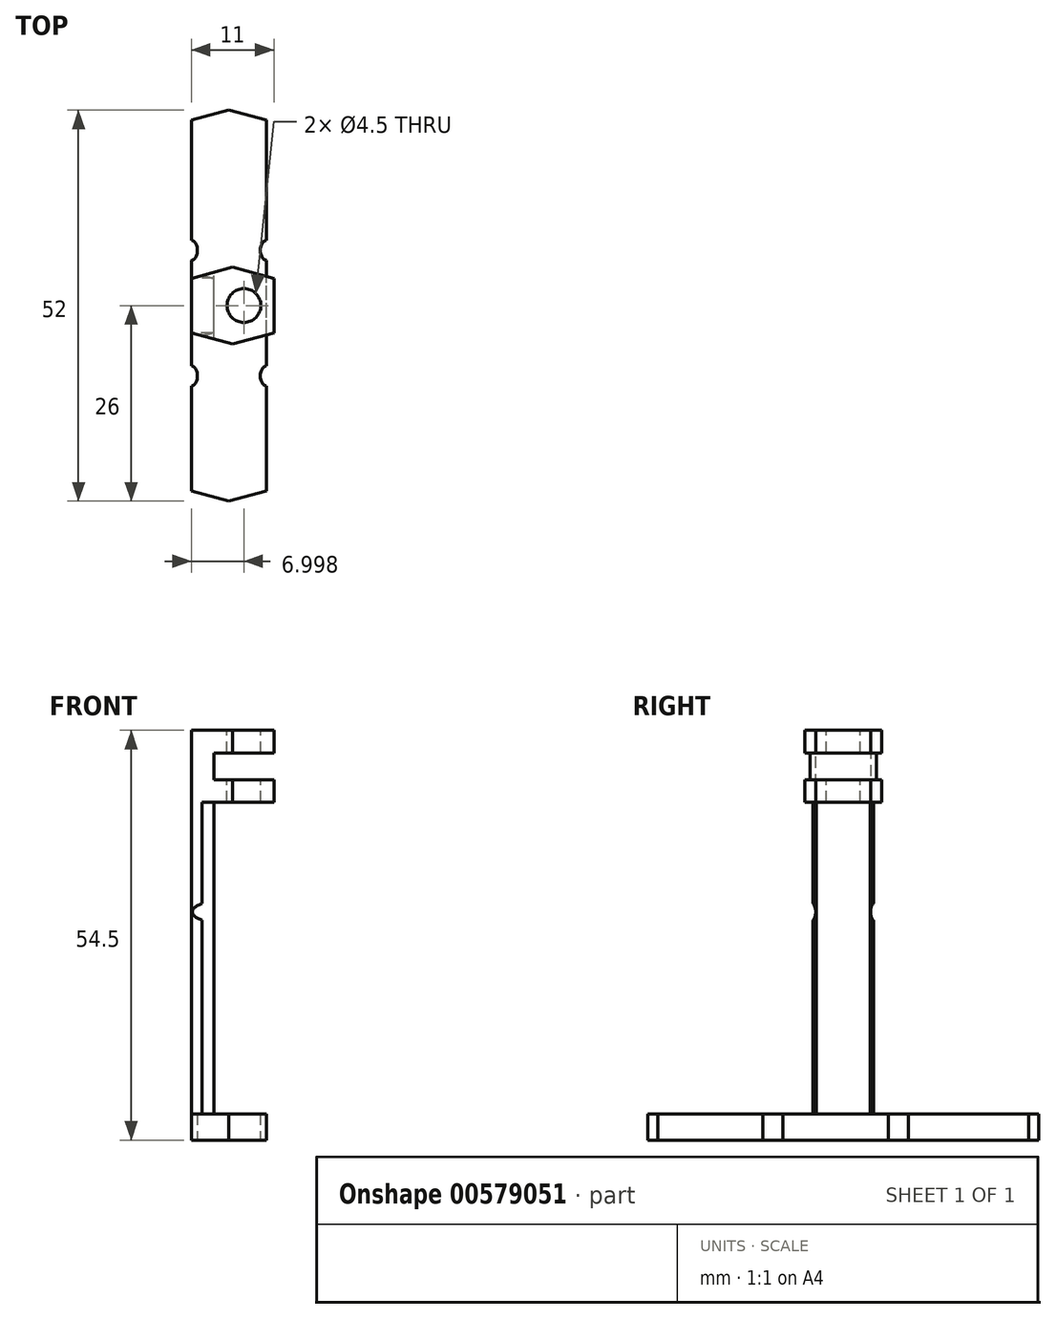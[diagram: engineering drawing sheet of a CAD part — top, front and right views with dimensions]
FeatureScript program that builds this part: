
annotation { "Feature Type Name" : "Feature", "Feature Type Description" : "" }
export const myFeature = defineFeature(function(context is Context, id is Id, definition is map)
    precondition{}
    {
        {
            var Q0;
            Q0=qCreatedBy(makeId("Front.planeOp"),FACE);
            var sketch = newSketch(context, id + "F0", { "sketchPlane" : qUnion([Q0])});
            skLineSegment(sketch, "E0.bottom", {"start": v(-42.95, 64.69) * mm, "end": v(-39.95, 64.69) * mm});
            skLineSegment(sketch, "E0.top", {"start": v(-42.95, 13.69) * mm, "end": v(-39.95, 13.69) * mm});
            skLineSegment(sketch, "E0.left", {"start": v(-42.95, 64.69) * mm, "end": v(-42.95, 13.69) * mm});
            skLineSegment(sketch, "E0.right", {"start": v(-39.95, 61.69) * mm, "end": v(-39.95, 58.14) * mm});
            skLineSegment(sketch, "E1.bottom", {"start": v(-39.95, 64.69) * mm, "end": v(-31.95, 64.69) * mm});
            skLineSegment(sketch, "E1.top", {"start": v(-39.95, 55.14) * mm, "end": v(-31.95, 55.14) * mm});
            skLineSegment(sketch, "E1.right", {"start": v(-31.95, 64.69) * mm, "end": v(-31.95, 58.14) * mm});
            skLineSegment(sketch, "E2.bottom", {"start": v(-39.95, 61.69) * mm, "end": v(-31.95, 61.69) * mm});
            skLineSegment(sketch, "E2.top", {"start": v(-39.95, 58.14) * mm, "end": v(-31.95, 58.14) * mm});
            skLineSegment(sketch, "E2.right", {"start": v(-31.95, 61.69) * mm, "end": v(-31.95, 58.14) * mm, "construction": true});
            skLineSegment(sketch, "E3", {"start": v(-31.95, 58.14) * mm, "end": v(-31.95, 55.14) * mm});
            skLineSegment(sketch, "E4.top", {"start": v(-42.95, 11.69) * mm, "end": v(-39.95, 11.69) * mm});
            skLineSegment(sketch, "E4.left", {"start": v(-42.95, 13.69) * mm, "end": v(-42.95, 11.69) * mm});
            skLineSegment(sketch, "E4.right", {"start": v(-39.95, 13.69) * mm, "end": v(-39.95, 11.69) * mm});
            skLineSegment(sketch, "E5.trimOffspring", {"start": v(-39.95, 55.14) * mm, "end": v(-39.95, 13.69) * mm});
            skLineSegment(sketch, "E6", {"start": v(-39.95, 58.14) * mm, "end": v(-39.95, 55.14) * mm});
            skLineSegment(sketch, "E7", {"start": v(-39.95, 64.69) * mm, "end": v(-39.95, 61.69) * mm});
            skSolve(sketch);
        }
        {
            var Q0;
            {var subQ0=sQuery(id+"F0.wireOp",EDGE,"E1.bottom");Q0=makeQuery(id+"F0.imprint","IMPRINT",FACE,{"disambiguationData":[TD([[makeQuery(id+"F0.imprint","IMPRINT",EDGE,{"derivedFrom":subQ0}),-1.0]])]});}
            var Q1;
            Q1=makeQuery(id+"F0.imprint","IMPRINT",FACE,{"disambiguationData":[TD([[makeQuery(id+"F0.imprint","IMPRINT",EDGE,{"derivedFrom":sQuery(id+"F0.wireOp",EDGE,"E1.top")}),1.0]])]});
            extrude(context, id + "F1", {"entities" : qUnion([Q0, Q1]), "endBound" : BoundingType.SYMMETRIC, "depth" : 11 * mm, "offsetDistance" : 25 * mm});
        }
        {
            var Q0;
            Q0=makeQuery(id+"F0.imprint","IMPRINT",FACE,{"disambiguationData":[TD([[makeQuery(id+"F0.imprint","IMPRINT",EDGE,{"derivedFrom":sQuery(id+"F0.wireOp",EDGE,"E0.bottom")}),-1.0]])]});
            extrude(context, id + "F2", {"entities" : qUnion([Q0]), "operationType" : NewBodyOperationType.ADD, "endBound" : BoundingType.SYMMETRIC, "depth" : 11 * mm, "offsetDistance" : 25 * mm});
        }
        {
            var Q0;
            Q0=makeQuery(id+"F2.opExtrude","CAP_EDGE",EDGE,{"disambiguationData":[OSD([sQuery(id+"F0.wireOp",EDGE,"E0.left")])],"isStart":true});
            var Q1;
            Q1=makeQuery(id+"F2.opExtrude","CAP_EDGE",EDGE,{"disambiguationData":[OSD([sQuery(id+"F0.wireOp",EDGE,"E0.left")])],"isStart":false});
            var Q2;
            Q2=makeQuery(id+"F1.opExtrude","CAP_EDGE",EDGE,{"disambiguationData":[OSD([sQuery(id+"F0.wireOp",EDGE,"E1.right")])],"isStart":false});
            var Q3;
            Q3=makeQuery(id+"F1.opExtrude","CAP_EDGE",EDGE,{"disambiguationData":[OSD([sQuery(id+"F0.wireOp",EDGE,"E3")])],"isStart":false});
            var Q4;
            Q4=makeQuery(id+"F1.opExtrude","CAP_EDGE",EDGE,{"disambiguationData":[OSD([sQuery(id+"F0.wireOp",EDGE,"E1.right")])],"isStart":true});
            var Q5;
            Q5=makeQuery(id+"F1.opExtrude","CAP_EDGE",EDGE,{"disambiguationData":[OSD([sQuery(id+"F0.wireOp",EDGE,"E3")])],"isStart":true});
            chamfer(context, id + "F3", {"entities" : qUnion([Q0, Q1, Q2, Q3, Q4, Q5]), "chamferType" : ChamferType.OFFSET_ANGLE, "width" : 7 * mm, "oppositeDirection" : true, "angle" : 15 * degree, "tangentPropagation" : true});
        }
        {
            var Q0;
            Q0=makeQuery(id+"F2.boolean.opBoolean","MERGE",FACE,{"derivedFrom":[makeQuery(id+"F1.opExtrude","SWEPT_FACE",FACE,{"disambiguationData":[OSD([sQuery(id+"F0.wireOp",EDGE,"E1.bottom")])]}),makeQuery(id+"F2.opExtrude","SWEPT_FACE",FACE,{"disambiguationData":[OSD([sQuery(id+"F0.wireOp",EDGE,"E0.bottom")])]})]});
            var sketch = newSketch(context, id + "F4", { "sketchPlane" : qUnion([Q0])});
            skCircle(sketch, "E8", {"center": v(-35.95, 0) * mm, "radius": 2.25 * mm});
            skSolve(sketch);
        }
        {
            var Q0;
            Q0=makeQuery(id+"F4.imprint","IMPRINT",FACE,{"disambiguationData":[TD([[makeQuery(id+"F4.imprint","IMPRINT",EDGE,{"derivedFrom":sQuery(id+"F4.wireOp",EDGE,"E8")}),1.0]])]});
            extrude(context, id + "F5", {"entities" : qUnion([Q0]), "operationType" : NewBodyOperationType.REMOVE, "oppositeDirection" : true, "depth" : 13.6 * mm, "offsetDistance" : 25 * mm});
        }
        {
            var Q0;
            {var subQ0=sQuery(id+"F0.wireOp",EDGE,"E6");var subQ3=sQuery(id+"F0.wireOp",EDGE,"E1.top");var subQ4=sQuery(id+"F0.wireOp",EDGE,"E7");var subQ8=sQuery(id+"F0.wireOp",EDGE,"E5.trimOffspring");var subQ10=sQuery(id+"F0.wireOp",EDGE,"E0.right");var subQ11=sQuery(id+"F0.wireOp",EDGE,"E0.left");Q0=makeQuery(id+"F3.opChamfer","BLEND_EDGE",EDGE,{"blendedFrom":[makeQuery(id+"F2.opExtrude","CAP_EDGE",EDGE,{"disambiguationData":[OSD([subQ11])],"isStart":false}),makeQuery(id+"F2.boolean.opBoolean","SPLIT",FACE,{"disambiguationData":[TD([makeQuery(id+"F1.opExtrude","SWEPT_FACE",FACE,{"disambiguationData":[OSD([subQ3])]})])],"derivedFrom":makeQuery(id+"F2.opExtrude","SWEPT_FACE",FACE,{"disambiguationData":[OSD([subQ10,subQ8,subQ0,subQ4])]})})],"blendedInto":[makeQuery(id+"F2.boolean.opBoolean","SPLIT",FACE,{"disambiguationData":[TD([makeQuery(id+"F1.opExtrude","SWEPT_FACE",FACE,{"disambiguationData":[OSD([subQ3])]})])],"derivedFrom":makeQuery(id+"F2.opExtrude","SWEPT_FACE",FACE,{"disambiguationData":[OSD([subQ10,subQ8,subQ0,subQ4])]})})]});}
            var Q1;
            {var subQ0=sQuery(id+"F0.wireOp",EDGE,"E6");var subQ3=sQuery(id+"F0.wireOp",EDGE,"E1.top");var subQ4=sQuery(id+"F0.wireOp",EDGE,"E7");var subQ8=sQuery(id+"F0.wireOp",EDGE,"E5.trimOffspring");var subQ10=sQuery(id+"F0.wireOp",EDGE,"E0.right");var subQ11=sQuery(id+"F0.wireOp",EDGE,"E0.left");Q1=makeQuery(id+"F3.opChamfer","BLEND_EDGE",EDGE,{"blendedFrom":[makeQuery(id+"F2.opExtrude","CAP_EDGE",EDGE,{"disambiguationData":[OSD([subQ11])],"isStart":true}),makeQuery(id+"F2.boolean.opBoolean","SPLIT",FACE,{"disambiguationData":[TD([makeQuery(id+"F1.opExtrude","SWEPT_FACE",FACE,{"disambiguationData":[OSD([subQ3])]})])],"derivedFrom":makeQuery(id+"F2.opExtrude","SWEPT_FACE",FACE,{"disambiguationData":[OSD([subQ10,subQ8,subQ0,subQ4])]})})],"blendedInto":[makeQuery(id+"F2.boolean.opBoolean","SPLIT",FACE,{"disambiguationData":[TD([makeQuery(id+"F1.opExtrude","SWEPT_FACE",FACE,{"disambiguationData":[OSD([subQ3])]})])],"derivedFrom":makeQuery(id+"F2.opExtrude","SWEPT_FACE",FACE,{"disambiguationData":[OSD([subQ10,subQ8,subQ0,subQ4])]})})]});}
            chamfer(context, id + "F6", {"entities" : qUnion([Q0, Q1]), "chamferType" : ChamferType.OFFSET_ANGLE, "width" : 1.6 * mm, "oppositeDirection" : true, "angle" : 30 * degree, "tangentPropagation" : true});
        }
        {
            var Q0;
            Q0=makeQuery(id+"F2.opExtrude","SWEPT_FACE",FACE,{"disambiguationData":[OSD([sQuery(id+"F0.wireOp",EDGE,"E0.top")])]});
            var sketch = newSketch(context, id + "F7", { "sketchPlane" : qUnion([Q0])});
            skLineSegment(sketch, "E9", {"start": v(-41.5, 4.01) * mm, "end": v(-41.5, -4.01) * mm, "construction": true});
            skLineSegment(sketch, "E10.bottom", {"start": v(-32.95, 26) * mm, "end": v(-42.95, 26) * mm});
            skLineSegment(sketch, "E10.top", {"start": v(-32.95, -26) * mm, "end": v(-42.95, -26) * mm});
            skLineSegment(sketch, "E10.left", {"start": v(-32.95, 26) * mm, "end": v(-32.95, -26) * mm});
            skLineSegment(sketch, "E10.right", {"start": v(-42.95, 26) * mm, "end": v(-42.95, -26) * mm});
            skPoint(sketch, "E10.middle", {"position": v(-41.5, 0) * mm});
            skSolve(sketch);
        }
        {
            var Q0;
            {var subQ6=sQuery(id+"F7.wireOp",EDGE,"E10.bottom");Q0=makeQuery(id+"F7.imprint","IMPRINT",FACE,{"disambiguationData":[TD([[makeQuery(id+"F7.imprint","IMPRINT",EDGE,{"derivedFrom":subQ6}),1.0]])]});}
            var Q1;
            {var subQ0=sQuery(id+"F0.wireOp",EDGE,"E0.top");var subQ1=makeQuery(id+"F2.opExtrude","SWEPT_FACE",FACE,{"disambiguationData":[OSD([subQ0])]});var subQ2=sQuery(id+"F0.wireOp",EDGE,"E0.left");var subQ3=makeQuery(id+"F2.opExtrude","CAP_EDGE",EDGE,{"disambiguationData":[OSD([subQ2])],"isStart":false});var subQ4=makeQuery(id+"F3.opChamfer","BLEND_EDGE",EDGE,{"blendedFrom":[subQ3,subQ1],"blendedInto":[subQ1]});Q1=makeQuery(id+"F7.imprint","IMPRINT",FACE,{"disambiguationData":[TD([[makeQuery(id+"F7.imprint","IMPRINT",EDGE,{"derivedFrom":subQ4}),1.0]])]});}
            extrude(context, id + "F8", {"entities" : qUnion([Q0, Q1]), "operationType" : NewBodyOperationType.ADD, "depth" : 3.5 * mm, "offsetDistance" : 25 * mm});
        }
        {
            var Q0;
            Q0=makeQuery(id+"F8.opExtrude","SWEPT_EDGE",EDGE,{"disambiguationData":[OSD([sQuery(id+"F7.wireOp",EDGE,"E10.bottom"),sQuery(id+"F7.wireOp",EDGE,"E10.right")])]});
            var Q1;
            Q1=makeQuery(id+"F8.opExtrude","SWEPT_EDGE",EDGE,{"disambiguationData":[OSD([sQuery(id+"F7.wireOp",EDGE,"E10.bottom"),sQuery(id+"F7.wireOp",EDGE,"E10.left")])]});
            var Q2;
            Q2=makeQuery(id+"F8.opExtrude","SWEPT_EDGE",EDGE,{"disambiguationData":[OSD([sQuery(id+"F7.wireOp",EDGE,"E10.top"),sQuery(id+"F7.wireOp",EDGE,"E10.right")])]});
            var Q3;
            Q3=makeQuery(id+"F8.opExtrude","SWEPT_EDGE",EDGE,{"disambiguationData":[OSD([sQuery(id+"F7.wireOp",EDGE,"E10.top"),sQuery(id+"F7.wireOp",EDGE,"E10.left")])]});
            chamfer(context, id + "F9", {"entities" : qUnion([Q0, Q1, Q2, Q3]), "chamferType" : ChamferType.OFFSET_ANGLE, "width" : 5 * mm, "oppositeDirection" : true, "angle" : 15 * degree, "tangentPropagation" : true});
        }
        {
            var Q0;
            Q0=makeQuery(id+"F8.opExtrude","CAP_FACE",FACE,{"disambiguationData":[OSD([sQuery(id+"F7.wireOp",EDGE,"E10.bottom"),sQuery(id+"F7.wireOp",EDGE,"E10.top"),sQuery(id+"F7.wireOp",EDGE,"E10.left"),sQuery(id+"F7.wireOp",EDGE,"E10.right")])],"isStart":false});
            var sketch = newSketch(context, id + "F10", { "sketchPlane" : qUnion([Q0])});
            skLineSegment(sketch, "E11", {"start": v(-42.95, 24.66) * mm, "end": v(-42.95, 9.36) * mm});
            skLineSegment(sketch, "E12", {"start": v(-42.95, 9.36) * mm, "end": v(-42.95, -7.35) * mm});
            skEllipticalArc(sketch, "E13", {});
            skEllipticalArc(sketch, "E14", {});
            skEllipticalArc(sketch, "E15", {});
            skEllipticalArc(sketch, "E16", {});
            skLineSegment(sketch, "E17", {"start": v(-32.95, 10.68) * mm, "end": v(-32.95, 8.04) * mm});
            skLineSegment(sketch, "E18", {"start": v(-32.95, 8.04) * mm, "end": v(-32.95, -8.67) * mm});
            skLineSegment(sketch, "E19", {"start": v(-32.95, -8.67) * mm, "end": v(-32.95, -6.03) * mm});
            skLineSegment(sketch, "E20", {"start": v(-42.95, -6.03) * mm, "end": v(-42.95, -8.67) * mm});
            const initialGuessF10  = {"E13": [-0.04295185990464106, -0.0073511903174221516, 0, -1, 0.0013188091106712818, 0.0008145245459041756, 0, 3.141592653589793], "E14": [-0.04295185990464106, 0.009362881071865569, 0, -1, 0.0013188091106712818, 0.0008145245459041756, 0, 3.141592653589793], "E15": [-0.032951859904641057, 0.009362881071865559, 0, -1, 0.0013188091106712818, 0.0008145245459041756, 3.141592653589793, 0], "E16": [-0.032951859904641057, -0.0073511903174221516, 0, -1, 0.001319, 0.0008145245459041756, 3.141592653589793, 0]};
            skSetInitialGuess(sketch, initialGuessF10);
            skSolve(sketch);
        }
        {
            var Q0;
            {var subQ3=sQuery(id+"F10.wireOp",EDGE,"E14");Q0=makeQuery(id+"F10.imprint","IMPRINT",FACE,{"disambiguationData":[TD([[makeQuery(id+"F10.imprint","IMPRINT",EDGE,{"derivedFrom":subQ3}),1.0]])]});}
            var Q1;
            {var subQ0=sQuery(id+"F10.wireOp",EDGE,"E13");Q1=makeQuery(id+"F10.imprint","IMPRINT",FACE,{"disambiguationData":[TD([[makeQuery(id+"F10.imprint","IMPRINT",EDGE,{"derivedFrom":subQ0}),1.0]])]});}
            var Q2;
            Q2=makeQuery(id+"F10.imprint","IMPRINT",FACE,{"disambiguationData":[TD([[makeQuery(id+"F10.imprint","IMPRINT",EDGE,{"derivedFrom":sQuery(id+"F10.wireOp",EDGE,"E16")}),1.0]])]});
            var Q3;
            Q3=makeQuery(id+"F10.imprint","IMPRINT",FACE,{"disambiguationData":[TD([[makeQuery(id+"F10.imprint","IMPRINT",EDGE,{"derivedFrom":sQuery(id+"F10.wireOp",EDGE,"E15")}),1.0]])]});
            extrude(context, id + "F11", {"entities" : qUnion([Q0, Q1, Q2, Q3]), "operationType" : NewBodyOperationType.REMOVE, "oppositeDirection" : true, "depth" : 18.1 * mm, "offsetDistance" : 25 * mm});
        }
        {
            var Q0;
            {var subQ0=sQuery(id+"F0.wireOp",EDGE,"E6");var subQ3=sQuery(id+"F0.wireOp",EDGE,"E1.top");var subQ4=sQuery(id+"F0.wireOp",EDGE,"E7");var subQ8=sQuery(id+"F0.wireOp",EDGE,"E5.trimOffspring");var subQ10=sQuery(id+"F0.wireOp",EDGE,"E0.right");Q0=makeQuery(id+"F2.boolean.opBoolean","SPLIT",FACE,{"disambiguationData":[TD([makeQuery(id+"F1.opExtrude","SWEPT_FACE",FACE,{"disambiguationData":[OSD([subQ3])]})])],"derivedFrom":makeQuery(id+"F2.opExtrude","SWEPT_FACE",FACE,{"disambiguationData":[OSD([subQ10,subQ8,subQ0,subQ4])]})});}
            var sketch = newSketch(context, id + "F12", { "sketchPlane" : qUnion([Q0])});
            skLineSegment(sketch, "E21", {"start": v(-3.6, 45.78) * mm, "end": v(3.6, 45.78) * mm});
            skEllipse(sketch, "E22", {"center": v(-4.47, 40.54) * mm, "majorRadius": 1.32 * mm, "minorRadius": 0.81 * mm, "majorAxis": v(0, -1)});
            skEllipse(sketch, "E23", {"center": v(4.44, 40.54) * mm, "majorRadius": 1.32 * mm, "minorRadius": 0.81 * mm, "majorAxis": v(0, -1)});
            skLineSegment(sketch, "E24", {"start": v(-4.47, 40.54) * mm, "end": v(4.44, 40.54) * mm});
            skSolve(sketch);
        }
        {
            var Q0;
            Q0=makeQuery(id+"F12.imprint","IMPRINT",FACE,{"disambiguationData":[TD([[makeQuery(id+"F12.imprint","IMPRINT",EDGE,{"derivedFrom":sQuery(id+"F12.wireOp",EDGE,"E22")}),1.0]])]});
            var Q1;
            Q1=makeQuery(id+"F12.imprint","IMPRINT",FACE,{"disambiguationData":[TD([[makeQuery(id+"F12.imprint","IMPRINT",EDGE,{"derivedFrom":sQuery(id+"F12.wireOp",EDGE,"E23")}),1.0]])]});
            extrude(context, id + "F13", {"entities" : qUnion([Q0, Q1]), "operationType" : NewBodyOperationType.REMOVE, "oppositeDirection" : true, "depth" : 25 * mm, "offsetDistance" : 25 * mm});
        }
    });
